# Revit family: 4LSS26337A75T-B,A2T-B
name_source: partatom
category: Plumbing Fixtures
units: mm (PartAtom-declared; Revit-internal decimal feet)

## family parameters
Always vertical = Yes
Cut with Voids When Loaded = No
OmniClass Number = 23.45.05.14.17
OmniClass Title = Showers
Part Type = Normal
Room Calculation Point = No
Round Connector Dimension = Use Diameter
Shared = No
Work Plane-Based = No

## types (4) — shared parameters
Assembly Code = D2010710
Keynote = 22 40 00.B3
Manufacturer = Best Bath Systems, Inc.
Type Comments = ADA Compliant
URL = http://www.best-bath.com
Unit Width = 63"

## per-type parameters (varying)
| type | Description | Threshold Height | Unit Height |
| 4LSS26337A75T | Smooth Wall Finish, Traditional Bull Nose Threshold | 3/4" | 81 1/4" |
| 4LSS26337A2T | Smooth Wall Finish, Traditional Bull Nose Threshold | 2" | 82 1/4" |
| 4LSS26337A75B | Smooth Wall Finish, Beveled Threshold | 3/4" | 81 1/4" |
| 4LSS26337A2B | Smooth Wall Finish, Beveled Threshold | 2" | 82 1/4" |

note: column(s) folded — value = type name in every type: Model

## geometry (parser evidence)
native form markers: Blend x26, Sweep x6
no freeform markers — native parametric forms only
